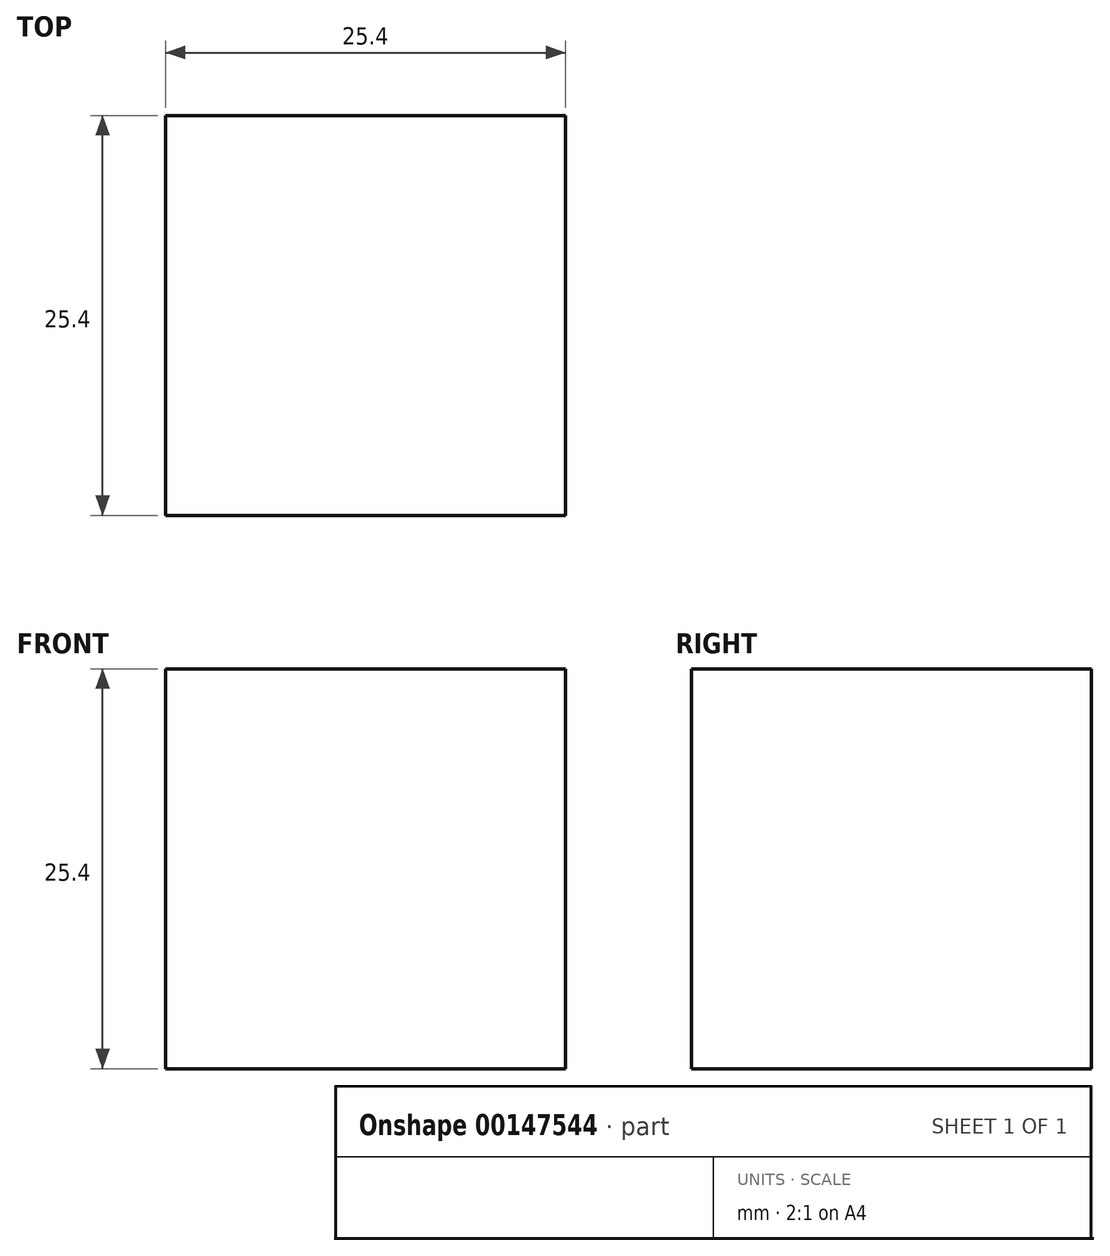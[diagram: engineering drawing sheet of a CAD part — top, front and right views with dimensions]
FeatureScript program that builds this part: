
annotation { "Feature Type Name" : "Feature", "Feature Type Description" : "" }
export const myFeature = defineFeature(function(context is Context, id is Id, definition is map)
    precondition{}
    {
        {
            var Q0;
            Q0=qCreatedBy(makeId("Top.planeOp"),FACE);
            var sketch = newSketch(context, id + "F0", { "sketchPlane" : qUnion([Q0])});
            skLineSegment(sketch, "E0.bottom", {"start": v(0, 0) * mm, "end": v(-25.4, 0) * mm});
            skLineSegment(sketch, "E0.top", {"start": v(0, -25.4) * mm, "end": v(-25.4, -25.4) * mm});
            skLineSegment(sketch, "E0.left", {"start": v(0, 0) * mm, "end": v(0, -25.4) * mm});
            skLineSegment(sketch, "E0.right", {"start": v(-25.4, 0) * mm, "end": v(-25.4, -25.4) * mm});
            skSolve(sketch);
        }
        {
            var Q0;
            Q0=qSketchRegion(id+"F0",true);
            extrude(context, id + "F1", {"entities" : qUnion([Q0]), "depth" : 25.4 * mm});
        }
    });
